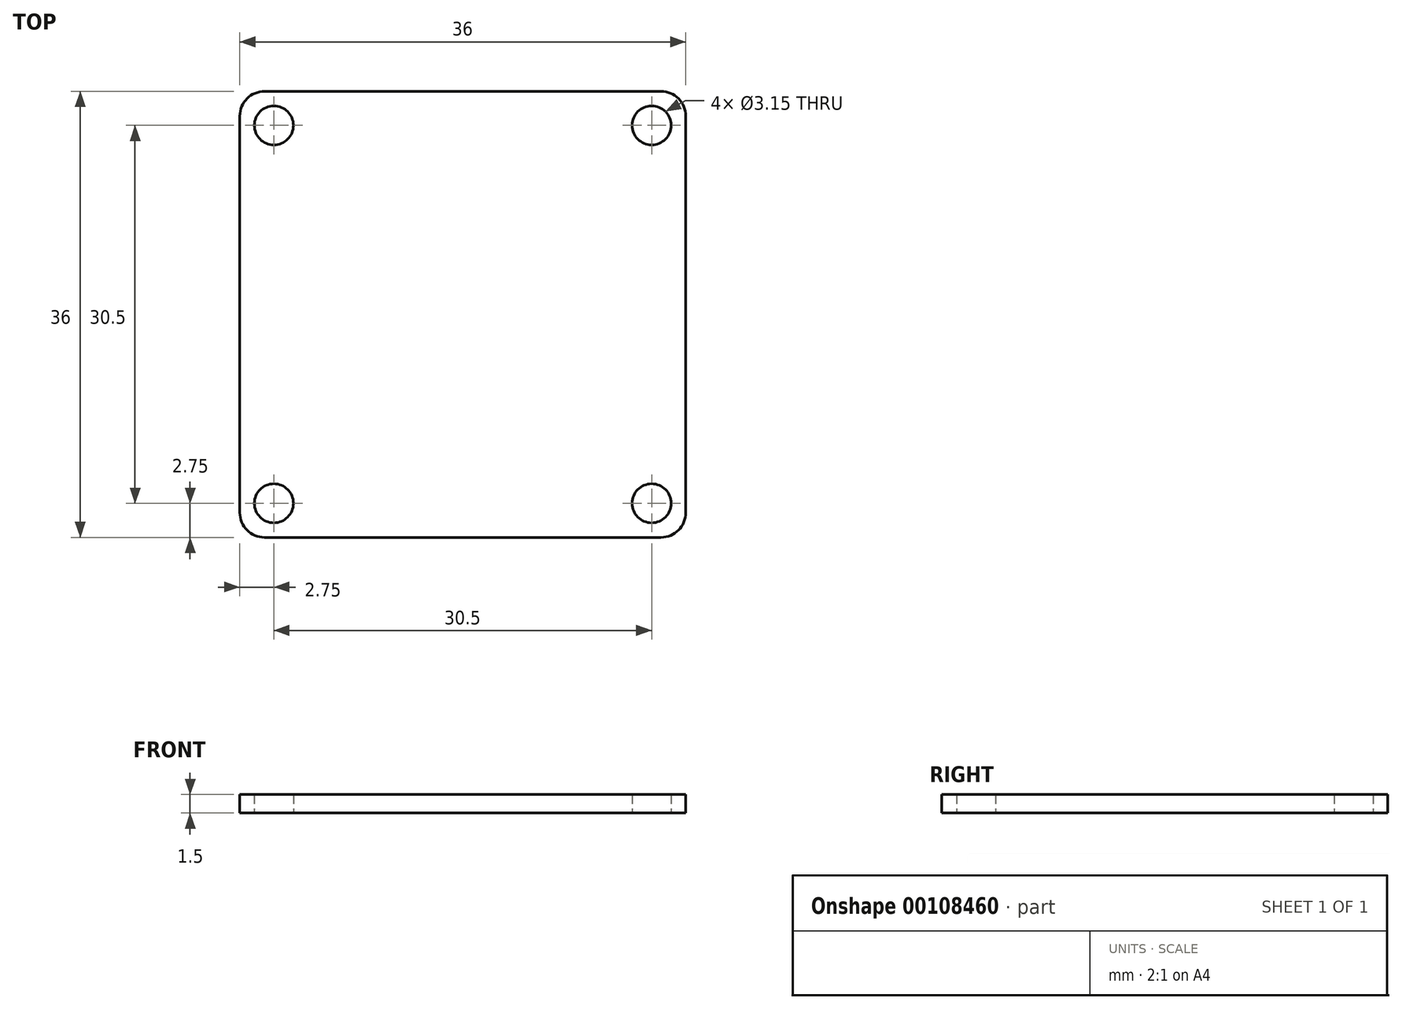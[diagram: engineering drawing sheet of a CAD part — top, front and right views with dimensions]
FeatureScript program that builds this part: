
annotation { "Feature Type Name" : "Feature", "Feature Type Description" : "" }
export const myFeature = defineFeature(function(context is Context, id is Id, definition is map)
    precondition{}
    {
        {
            var Q0;
            Q0=qCreatedBy(makeId("Top.planeOp"),FACE);
            var sketch = newSketch(context, id + "F0", { "sketchPlane" : qUnion([Q0])});
            skLineSegment(sketch, "E0.bottom", {"start": v(16, 18) * mm, "end": v(-16, 18) * mm});
            skLineSegment(sketch, "E0.top", {"start": v(16, -18) * mm, "end": v(-16, -18) * mm});
            skLineSegment(sketch, "E0.left", {"start": v(18, 16) * mm, "end": v(18, -16) * mm});
            skLineSegment(sketch, "E0.right", {"start": v(-18, 16) * mm, "end": v(-18, -16) * mm});
            skPoint(sketch, "E0.middle", {"position": v(0, 0) * mm});
            skPoint(sketch, "E1.visualSharp", {"position": v(-18, -18) * mm});
            skArc(sketch, "E1.filletArc", {"start": v(-18, -16) * mm, "mid": v(-17.41, -17.41) * mm, "end": v(-16, -18) * mm});
            skPoint(sketch, "E2.visualSharp", {"position": v(-18, 18) * mm});
            skArc(sketch, "E2.filletArc", {"start": v(-16, 18) * mm, "mid": v(-17.41, 17.41) * mm, "end": v(-18, 16) * mm});
            skPoint(sketch, "E3.visualSharp", {"position": v(18, 18) * mm});
            skArc(sketch, "E3.filletArc", {"start": v(18, 16) * mm, "mid": v(17.41, 17.41) * mm, "end": v(16, 18) * mm});
            skPoint(sketch, "E4.visualSharp", {"position": v(18, -18) * mm});
            skArc(sketch, "E4.filletArc", {"start": v(16, -18) * mm, "mid": v(17.41, -17.41) * mm, "end": v(18, -16) * mm});
            skLineSegment(sketch, "E5.bottom", {"start": v(-15.25, 15.25) * mm, "end": v(15.25, 15.25) * mm, "construction": true});
            skLineSegment(sketch, "E5.top", {"start": v(-15.25, -15.25) * mm, "end": v(15.25, -15.25) * mm, "construction": true});
            skLineSegment(sketch, "E5.left", {"start": v(-15.25, 15.25) * mm, "end": v(-15.25, -15.25) * mm, "construction": true});
            skLineSegment(sketch, "E5.right", {"start": v(15.25, 15.25) * mm, "end": v(15.25, -15.25) * mm, "construction": true});
            skSolve(sketch);
        }
        {
            var Q0;
            Q0 = qSketchRegion(id + "F0", true);
            extrude(context, id + "F1", {"entities" : qUnion([Q0]), "depth" : 1.5 * mm});
        }
        {
            var Q0;
            Q0=sQuery(id+"F0.wireOp",VERTEX,"E5.bottom.start");
            var Q1;
            Q1=sQuery(id+"F0.wireOp",VERTEX,"E5.top.start");
            var Q2;
            Q2=sQuery(id+"F0.wireOp",VERTEX,"E5.right.end");
            var Q3;
            Q3=sQuery(id+"F0.wireOp",VERTEX,"E5.right.start");
            var Q4;
            Q4=makeQuery(id+"F1.opExtrude","SWEPT_BODY",BODY,{"disambiguationData":[OSD([sQuery(id+"F0.wireOp",EDGE,"E0.bottom"),sQuery(id+"F0.wireOp",EDGE,"E0.top"),sQuery(id+"F0.wireOp",EDGE,"E0.left"),sQuery(id+"F0.wireOp",EDGE,"E0.right"),sQuery(id+"F0.wireOp",EDGE,"E1.filletArc"),sQuery(id+"F0.wireOp",EDGE,"E2.filletArc"),sQuery(id+"F0.wireOp",EDGE,"E3.filletArc"),sQuery(id+"F0.wireOp",EDGE,"E4.filletArc")])]});
            hole(context, id + "F2", {"style" : HoleStyle.SIMPLE, "endStyle" : HoleEndStyle.THROUGH, "oppositeDirection" : true, "standardTappedOrClearance" : lookupTablePath({ "standard" : "ISO", "fit" : "Close", "size" : "M3", "type" : "Clearance" }), "standardBlindInLast" : lookupTablePath({ "fit" : "Close", "standard" : "ISO", "size" : "M3", "type" : "Clearance" }), "holeDiameter" : 3.15 * mm, "startFromSketch" : true, "locations" : qUnion([Q0, Q1, Q2, Q3]), "scope" : qUnion([Q4]), "isTappedThrough" : true});
        }
    });
